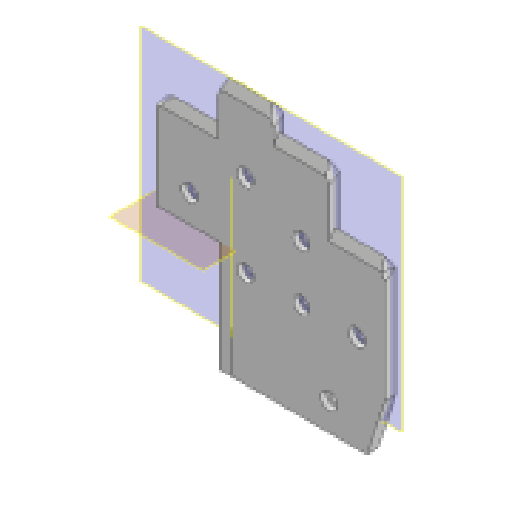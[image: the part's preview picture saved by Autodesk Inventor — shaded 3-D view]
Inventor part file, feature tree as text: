
AUTODESK INVENTOR PART (.ipt)
format: ipt  version: 2025 (Build 290162010, 162A)  size: 323,584 bytes
history: native  units: in
note: dims shown in document units (in); Inventor stores cm internally (conversion verified against a paired STEP export)
features: reference x33, extrude x21, sketch x21, other x17, plane x3, projected_geometry x1
ambient origin geometry x8: Origin, YZ Plane, XZ Plane, XY Plane, X Axis, Y Axis, Z Axis, Center Point
bodies: Solid1 (feature_tree)
feature tree (96):
  extrude  "Extrusion1"  Depth=0.2in TaperAngle=0.0deg
  extrude  "Extrusion3"  Depth=2.625in TaperAngle=0.0deg
  sketch  "Sketch4"  dims[d24=0.4375in d25=0.0in d26=0.75in d27=0.0in]
  extrude  "Extrusion4"  Depth=0.75in TaperAngle=0.0deg
  extrude  "Extrusion5"  Depth=0.5625in TaperAngle=0.0deg
  extrude  "Extrusion6"  Depth=0.5625in TaperAngle=0.0deg
  extrude  "Extrusion7"  Depth=0.14in
  extrude  "Extrusion8"  Depth=0.14in
  extrude  "Extrusion9"  Depth=0.505in
  extrude  "Extrusion10"  Depth=1.0in
  extrude  "Extrusion11"  Depth=0.14in
  extrude  "Extrusion12"  Depth=1.0in
  plane  "Work Plane1"
  extrude  "Extrusion15"  Depth=0.505in
  plane  "Work Plane2"
  extrude  "Extrusion16"  Depth=5.0in TaperAngle=0.0deg
  extrude  "Extrusion18"  Depth=0.3in
  plane  "Work Plane3"
  extrude  "Extrusion20"  Depth=0.3in
  extrude  "Extrusion21"  Depth=0.3in
  extrude  "Extrusion22"  Depth=5.0in TaperAngle=0.0deg
  extrude  "Extrusion23"  [1 undecoded]
  extrude  "Extrusion24"  Depth=0.925in TaperAngle=0.0deg
  extrude  "Extrusion25"  Depth=0.2in TaperAngle=0.0deg
  extrude  "Extrusion26"  Depth=0.1in
  sketch  "Sketch1"  dims[d1=1.25in d2=1.533in d3=1.164in d4=0.463in d5=0.1358in d6=1.121in d7=0.8in d8=1.01in d9=1.01in d10=1.01in d11=0.4in d12=1.0in d13=0.2in d14=0.0in d18=2.25in d19=0.0in]
  sketch  "Sketch3"  dims[d20=1.75in d21=0.0in d22=2.625in d23=0.0in]
  reference  "Reference1"
  reference  "Reference2"
  sketch  "Sketch5"  dims[d28=1.0in d29=0.0in d30=0.5625in d31=0.0in]
  reference  "Reference3"
  sketch  "Sketch6"  dims[d32=0.5625in d33=0.0in d34=0.5625in d35=0.0in]
  reference  "Reference4"
  reference  "Reference5"
  sketch  "Sketch7"  dims[d36=1.1875in d37=0.0in d38=0.14in]
  reference  "Reference6"
  sketch  "Sketch8"  dims[d39=0.14in d40=0.14in]
  reference  "Reference7"
  sketch  "Sketch9"  dims[d41=0.505in d42=0.505in]
  reference  "Reference8"
  reference  "Reference9"
  sketch  "Sketch10"  dims[d43=0.505in d44=1.0in]
  reference  "Reference10"
  sketch  "Sketch11"  dims[d45=0.14in d46=0.14in]
  reference  "Reference11"
  reference  "Reference12"
  sketch  "Sketch12"  dims[d47=1.5in d48=1.0in]
  reference  "Reference13"
  reference  "Reference14"
  reference  "Reference15"
  reference  "Reference16"
  sketch  "Sketch13"  dims[d53=0.14in d54=0.505in]
  reference  "Reference17"
  reference  "Reference18"
  reference  "Reference19"
  reference  "Reference20"
  reference  "Reference21"
  reference  "Reference24"
  sketch  "Sketch17"  dims[d55=0.5in d56=5.0in d57=5.0in d58=0.0in d59=0.0in]
  sketch  "Sketch18"  dims[d60=-0.1in d61=0.3in]
  reference  "Reference25"
  reference  "Reference26"
  reference  "Reference27"
  sketch  "Sketch20"  dims[d62=0.3in d63=0.3in]
  reference  "Reference28"
  sketch  "Sketch21"  dims[d64=0.3in d65=0.3in]
  reference  "Reference29"
  sketch  "Sketch22"  dims[d66=0.3in d67=5.0in d68=0.0in]
  reference  "Reference30"
  reference  "Reference31"
  reference  "Reference32"
  reference  "Reference33"
  sketch  "Sketch23"  dims[d71=5.0in d72=0.0in d75=-2.75in]
  projected_geometry  "Projected Loop2"
  sketch  "Sketch24"  dims[d76=1.0in d77=0.0in d78=0.925in d79=0.0in]
  reference  "Reference34"
  reference  "Reference35"
  sketch  "Sketch25"  dims[d80=0.2in d81=0.0in d82=0.2in d83=0.0in]
  sketch  "Sketch26"  dims[d84=0.14in d85=0.71in d86=0.355in d87=0.5in d88=1.3125in d89=0.0in d90=0.3in d91=0.1in d92=0.0in d93=1.0in d94=0.0in]
  parser-record x1  (decoder bookkeeping rows leaked as tree rows — omitted from the tree; the rows remain in map.json)
  other  "Hand Assem.iam"
  other  "Wrist Base:1"
  other  "Finger Assem:2"
  other  "Servo Base:1"
  other  "Thumb Base2:1"
  other  "KNUCKLE 4:1"
  other  "Finger Assem:3"
  other  "Finger Assem:1"
  other  "KNUCKLE 1:1"
  other  "PALM 1:1"
  other  "Finger Assem:4"
  other  "KNUCKLE 2:1"
  other  "PALM 2:1"
  other  "KNUCKLE 3:1"
  other  "PALM 3:1"
  other  "PALM 4:1"
note: 1 required parameter value undecoded (feature->parameter linkage not recoverable at this tier; creation-order binding heuristic only, values carry confidence <= 0.55)
note: 1 file-system path scrubbed to <path> (originals preserved in map.json)
